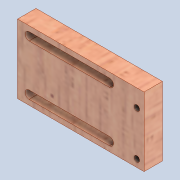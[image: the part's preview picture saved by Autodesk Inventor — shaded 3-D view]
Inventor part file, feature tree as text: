
AUTODESK INVENTOR PART (.ipt)
format: ipt  version: 2020 (Build 240168000, 168)  size: 202,240 bytes
history: native  units: mm
features: extrude x2, sketch x2, hole x1
ambient origin geometry x8: Origin, YZ Plane, XZ Plane, XY Plane, X Axis, Y Axis, Z Axis, Center Point
bodies: Solid1 (feature_tree)
feature tree (5):
  extrude  "Extrusion1"  Depth=30.0mm
  extrude  "Extrusion5"  Depth=3.5mm
  hole  "Hole1"  [1 undecoded]
  sketch  "Sketch1"  dims[d0=55.0mm d1=30.0mm]
  sketch  "Sketch5"  dims[d2=8.0mm d3=0.0mm d29=3.5mm d30=4.0mm d31=4.0mm d33=35.0mm d34=10.0mm d35=0.0mm d36=5.0mm d37=2.459mm d38=8.0mm d39=4.0mm d40=2.0mm d41=90.0deg d42=8.0mm d43=20.594885mm d44=3.1275mm]
note: 1 required parameter value undecoded (feature->parameter linkage not recoverable at this tier; creation-order binding heuristic only, values carry confidence <= 0.55)
